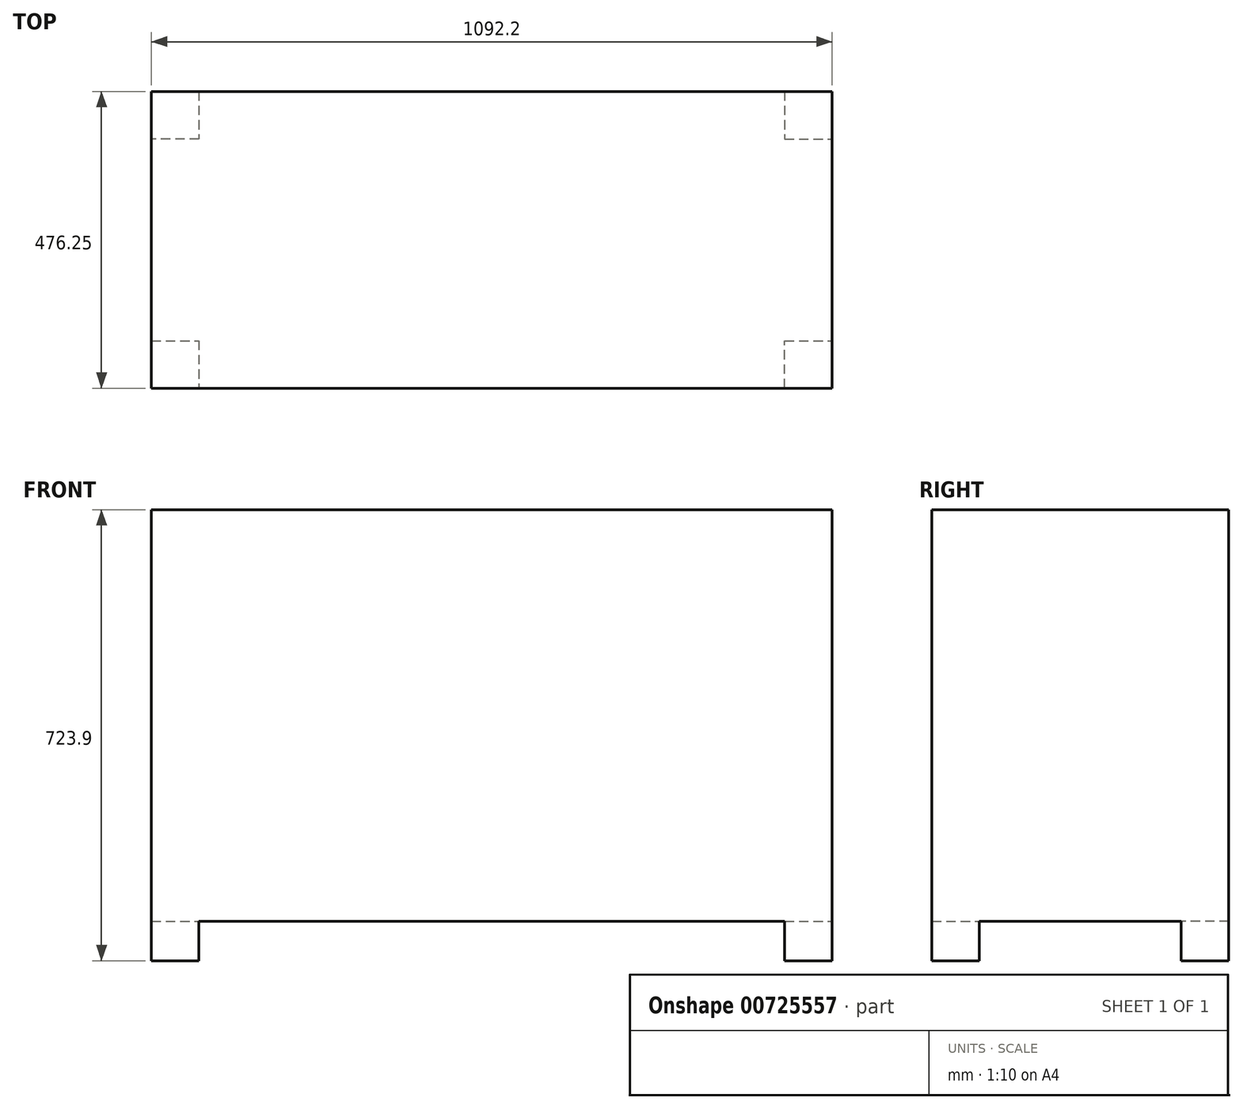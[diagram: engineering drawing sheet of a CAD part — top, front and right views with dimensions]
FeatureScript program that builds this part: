
annotation { "Feature Type Name" : "Feature", "Feature Type Description" : "" }
export const myFeature = defineFeature(function(context is Context, id is Id, definition is map)
    precondition{}
    {
        {
            var Q0;
            Q0=qCreatedBy(makeId("Top.planeOp"),FACE);
            var sketch = newSketch(context, id + "F0", { "sketchPlane" : qUnion([Q0])});
            skLineSegment(sketch, "E0.bottom", {"start": v(0, 0) * mm, "end": v(1092.2, 0) * mm});
            skLineSegment(sketch, "E0.top", {"start": v(0, 476.25) * mm, "end": v(1092.2, 476.25) * mm});
            skLineSegment(sketch, "E0.left", {"start": v(0, 0) * mm, "end": v(0, 476.25) * mm});
            skLineSegment(sketch, "E0.right", {"start": v(1092.2, 0) * mm, "end": v(1092.2, 476.25) * mm});
            skSolve(sketch);
        }
        {
            var Q0;
            Q0=makeQuery(id+"F0.imprint","IMPRINT",FACE,{"disambiguationData":[TD([[makeQuery(id+"F0.imprint","IMPRINT",EDGE,{"derivedFrom":sQuery(id+"F0.wireOp",EDGE,"E0.bottom")}),1.0]])]});
            extrude(context, id + "F1", {"entities" : qUnion([Q0]), "depth" : 723.9 * mm, "offsetDistance" : 25.4 * mm});
        }
        {
            var Q0;
            Q0=makeQuery(id+"F1.opExtrude","CAP_FACE",FACE,{"disambiguationData":[OSD([sQuery(id+"F0.wireOp",EDGE,"E0.bottom"),sQuery(id+"F0.wireOp",EDGE,"E0.top"),sQuery(id+"F0.wireOp",EDGE,"E0.left"),sQuery(id+"F0.wireOp",EDGE,"E0.right")])],"isStart":true});
            var sketch = newSketch(context, id + "F2", { "sketchPlane" : qUnion([Q0])});
            skLineSegment(sketch, "E1", {"start": v(0, -76.2) * mm, "end": v(76.2, -76.2) * mm});
            skLineSegment(sketch, "E2", {"start": v(76.2, -76.2) * mm, "end": v(76.2, 0) * mm});
            skLineSegment(sketch, "E3", {"start": v(1016, 0) * mm, "end": v(1016, -76.2) * mm});
            skLineSegment(sketch, "E4", {"start": v(1016, -76.2) * mm, "end": v(1092.2, -76.2) * mm});
            skLineSegment(sketch, "E5", {"start": v(1016, -476.25) * mm, "end": v(1016, -400.05) * mm});
            skLineSegment(sketch, "E6", {"start": v(1016, -400.05) * mm, "end": v(1092.2, -400.05) * mm});
            skLineSegment(sketch, "E7", {"start": v(76.2, -476.25) * mm, "end": v(76.2, -400.05) * mm});
            skLineSegment(sketch, "E8", {"start": v(76.2, -400.05) * mm, "end": v(0, -400.05) * mm});
            skSolve(sketch);
        }
        {
            var Q0;
            Q0 = qSketchRegion(id + "F2", true);
            var Q1;
            {var subQ7=sQuery(id+"F2.wireOp",EDGE,"E1");Q1=makeQuery(id+"F2.imprint","IMPRINT",FACE,{"disambiguationData":[TD([[makeQuery(id+"F2.imprint","IMPRINT",EDGE,{"derivedFrom":subQ7}),-1.0]])]});}
            extrude(context, id + "F3", {"entities" : qUnion([Q0, Q1]), "operationType" : NewBodyOperationType.REMOVE, "oppositeDirection" : true, "depth" : 63.5 * mm, "offsetDistance" : 25.4 * mm});
        }
    });
